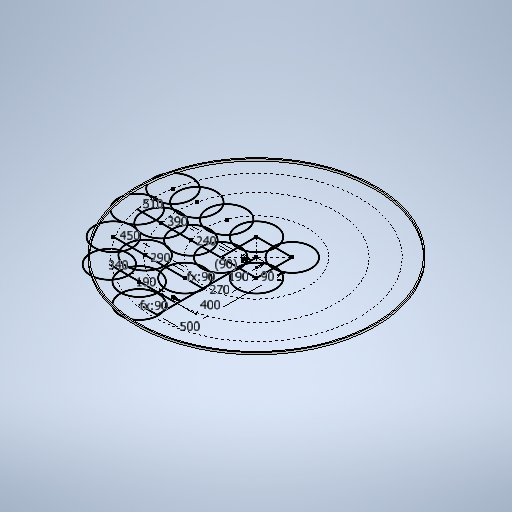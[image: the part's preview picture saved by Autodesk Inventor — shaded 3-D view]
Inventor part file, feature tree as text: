
AUTODESK INVENTOR PART (.ipt)
format: ipt  version: 2025.1 (Build 291241020, 241B)  size: 320,000 bytes
history: native  units: mm
features: sketch x3, extrude x1
ambient origin geometry x8: Origin, YZ Plane, XZ Plane, XY Plane, X Axis, Y Axis, Z Axis, Center Point
bodies: Solid1 (feature_tree)
feature tree (4):
  extrude  "Extrusion1"  Depth=6.0mm
  sketch  "Sketch2"  dims[d2=10.0mm d3=0.0mm]
  sketch  "Sketch3"  dims[d4=190.0mm d7=90.0mm d8=270.0mm d9=400.0mm d10=500.0mm d11=240.0mm d12=390.0mm d13=510.0mm d14=90.0mm d15=90.0mm d16=290.0mm d17=450.0mm d18=190.0mm d19=340.0mm d20=90.0mm d21=190.0mm d22=1200.0mm]
  sketch  "Sketch1"  dims[d0=1200.0mm d1=6.0mm]
